# Revit family: IS_Tempo_T0565_BIM_NL
name_source: partatom
category: Plumbing Fixtures
revit_build: Autodesk Revit 2017 (Build: 20171027_0315(x64)
units: mm (PartAtom-declared; Revit-internal decimal feet)

## family parameters
Cut with Voids When Loaded = No
Host = Face
OmniClass Number = 23.45.05.14.14
OmniClass Title = Sinks/Lavatories
Part Type = Normal
Room Calculation Point = No
Round Connector Dimension = Use Diameter
Shared = Yes

## types (1)
- T056501 - NOUVEAU WASTAFEL 55X45 MET KRAANGAT/OVERLOOP
    Accessories = www.idealstandardnederland.nl
    AreaUnits = millimeters
    Assembly Code = C1030200
    AssetType = Fixed
    BIMObjectName = NBS_WashBasinAssembly_WallMounted
    BarCode = 8014140410140
    Brand = Ideal Standard
    CWFU = 0
    CodePerformance = DIN EN 14688, DIN EN 31
    Color = Wit
    ConnectionType = Sanitair
    Cost = 0 $
    Default Elevation = 800 mm  [stored 2.62467 ft]
    Description = Nouveau wastafel 550 mm van keramiek. Vervaardigd volgens DIN EN 31 en DIN EN 14688. 1 kraangat midden doorgestoken. Met overloop. Bevestiging met 2 schroeven M10 x 140 mm (K710767). Exclusief bevestigingsmateriaal.
    DrainSize = 46 mm  [stored 0.150919 ft]
    DurationUnit = year
    ECA = No
    ExpectedLife = 30
    Features = Wastafel 550 mm van keramiek. Vervaardigd volgens DIN EN 31 en DIN EN 14688. 1 kraangat midden doorgestoken. Met overloop. Bevestiging met 2 schroeven M10 x 140 mm (K710767). Exclusief bevestigingsmateriaal.
    Finish = Wit
    HWFU = 0
    IfcExportAs = IfcSanitaryType
    IfcExportType = WASHHANDBASIN
    InstallationInstructions = http://www.idealstandardnederland.nl
    LinearUnits = millimeters
    ManufacturerURL = www.idealstandardnederland.nl
    Material = Keramiek
    Model = T056501
    ModelNumber = T056501
    ModelReference = Nouveau wastafel 550 mm van keramiek. Vervaardigd volgens DIN EN 31 en DIN EN 14688. 1 kraangat midden doorgestoken. Met overloop. Bevestiging met 2 schroeven M10 x 140 mm (K710767). Exclusief bevestigingsmateriaal.
    NBSReference = 45-35-70/???
    Name = NOUVEAU WASTAFEL 55X45 MET KRAANGAT/OVERLOOP
    NettWeight = 15,7 kg
    NominalDepth = 451 mm
    NominalHeight = 187 mm
    NominalLength = 0 mm  [stored 0 ft]
    NominalWidth = 551 mm
    ProductInformation = http://www.idealstandardnederland.nl
    Shape = Sculptured
    Size = 550 x 450 x 187 mm
    Space = Internal
    URL = www.idealspec.nl
    Uniclass2015Code = Pr_40_20_96
    Uniclass2015Title = Wall-hung wash basins
    Version = 1
    VolumeUnits = Litres
    WFU = 0
    WRAS = No
    WarrantyDescription = Fabrieksgarantie
    WarrantyDurationParts = 5
    WarrantyDurationUnit = jaar
    WashHandBasinMounting = Wandhangend
    WashHandBasinType = Wastafel
    WaterEfficientProduct = No

note: [stored X ft] marks values corroborated as IEEE doubles in the binary element streams (Revit-internal decimal feet)

## geometry (parser evidence)
native form markers: Sweep x4
no freeform markers — native parametric forms only
